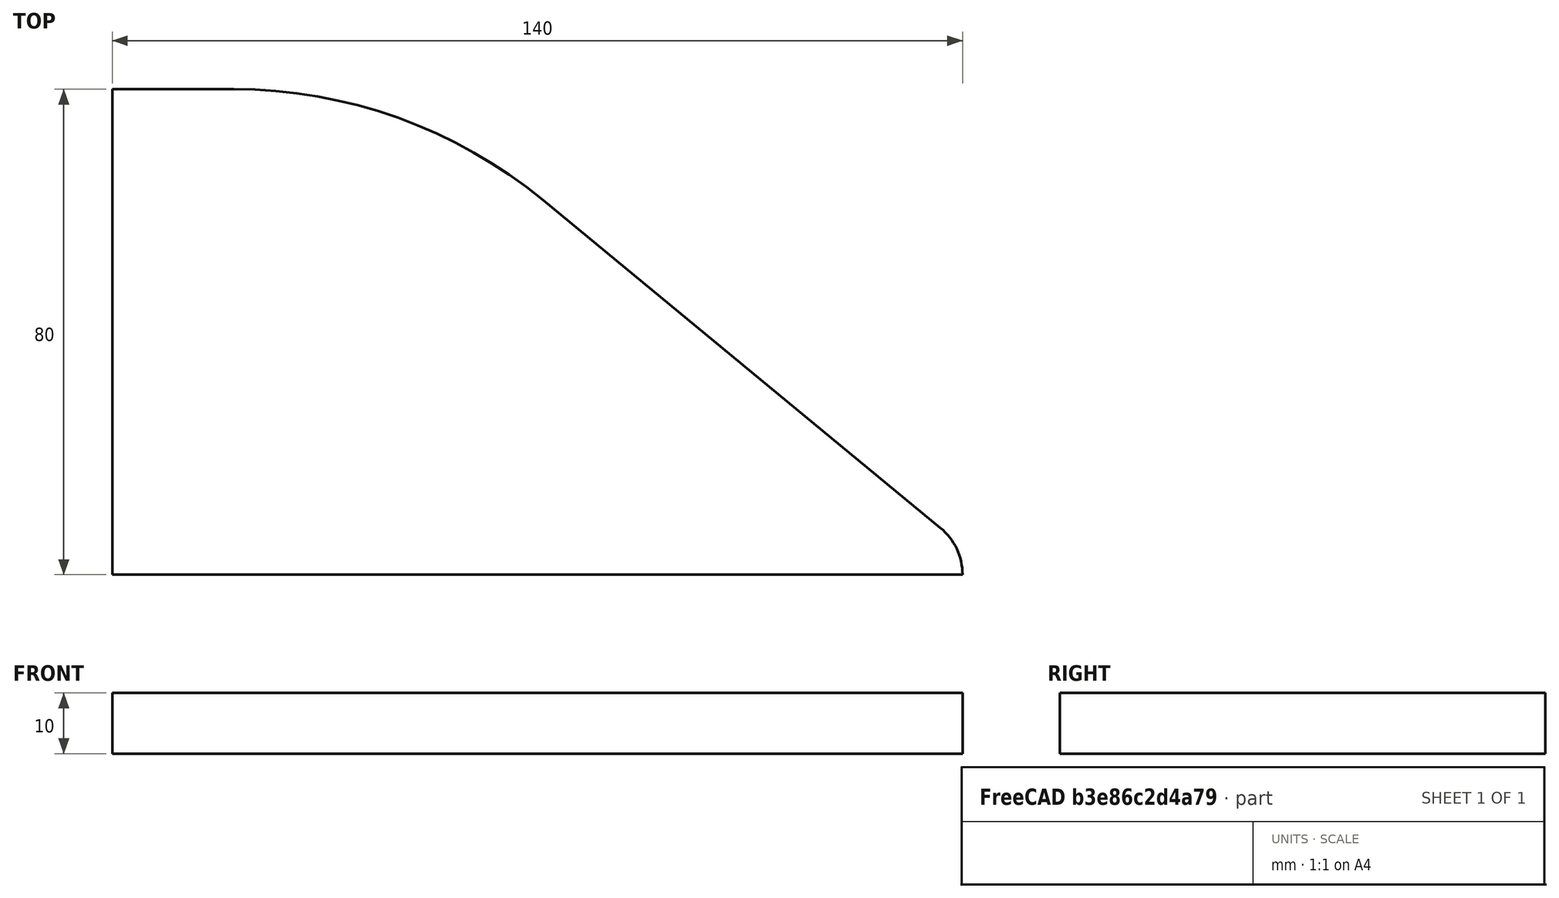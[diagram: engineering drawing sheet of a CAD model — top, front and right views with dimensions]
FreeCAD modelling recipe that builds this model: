
FCSTD DOCUMENT  (FreeCAD 0.16R6706 (Git))
Label: guide_air_paroie_exterieure
License: All rights reserved
LicenseURL: http://en.wikipedia.org/wiki/All_rights_reserved
objects: Sketcher::SketchObject×1, PartDesign::Pad×1
note: 3 computed .brp shape members not serialized (recipe doc carries the construction recipe); baked Part::Feature solids carry a one-line shape summary decoded from their .brp

FEATURE [Sketcher::SketchObject] Sketch
  sketch-geometry (6):
    g0: LineSegment StartX=0 StartY=0 StartZ=0 EndX=140 EndY=0 EndZ=0
    g1: LineSegment StartX=0 StartY=0 StartZ=0 EndX=0 EndY=80 EndZ=0
    g2: LineSegment StartX=0 StartY=80 StartZ=0 EndX=20 EndY=80 EndZ=0
    g3: LineSegment StartX=70.909 StartY=61.7112 StartZ=0 EndX=136.364 EndY=7.71389 EndZ=0
    g4: ArcOfCircle CenterX=20 CenterY=0 CenterZ=0 NormalX=0 NormalY=0 NormalZ=1 Radius=80 StartAngle=0.881022 EndAngle=1.5708
    g5: ArcOfCircle CenterX=130 CenterY=0 CenterZ=0 NormalX=0 NormalY=0 NormalZ=1 Radius=10 StartAngle=0 EndAngle=0.881021
  constraints (18):
    c: Horizontal(g0)
    c: Vertical(g1)
    c: Horizontal(g2)
    c: Coincident(g1,g-1)
    c: Coincident(g0,g-1)
    c: Coincident(g1,g2)
    c: Coincident(g4,g2)
    c: Coincident(g4,g3)
    c: Tangent(g4,g2)
    c: Tangent(g3,g4)
    c: Tangent(g5,g3) = 1.5708
    c: Coincident(g0,g5)
    c: DistanceX(g0,g0) = 140
    c: PointOnObject(g5,g0)
    c: DistanceX(g-1,g5) = 130
    c: DistanceX(g-1,g4) = 20
    c: DistanceY(g1,g1) = 80
    c: PointOnObject(g4,g0)
FEATURE [PartDesign::Pad] Pad
  Length = 10
  Length2 = 100
  Sketch = -> Sketch
  Type = 0
